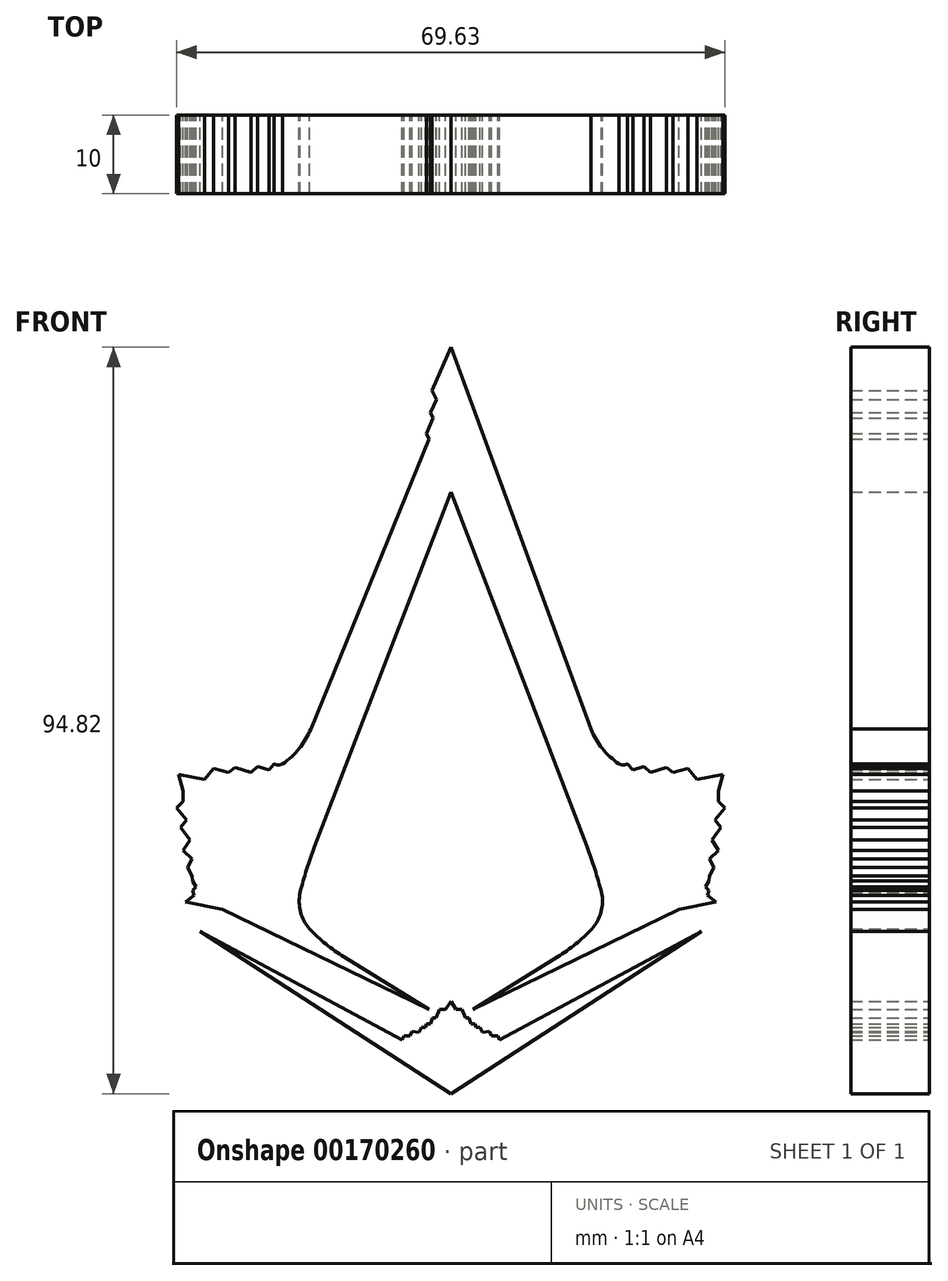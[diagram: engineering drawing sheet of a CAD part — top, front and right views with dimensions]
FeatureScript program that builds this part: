
annotation { "Feature Type Name" : "Feature", "Feature Type Description" : "" }
export const myFeature = defineFeature(function(context is Context, id is Id, definition is map)
    precondition{}
    {
        {
            var Q0;
            Q0=qCreatedBy(makeId("Front.planeOp"),FACE);
            var sketch = newSketch(context, id + "F0", { "sketchPlane" : qUnion([Q0])});
            skLineSegment(sketch, "E0", {"start": v(-37.8, 97.98) * mm, "end": v(-40.16, 92.47) * mm});
            skLineSegment(sketch, "E1", {"start": v(-40.16, 92.47) * mm, "end": v(-39.64, 91.37) * mm});
            skLineSegment(sketch, "E2", {"start": v(-39.64, 91.37) * mm, "end": v(-40.37, 89.66) * mm});
            skLineSegment(sketch, "E3", {"start": v(-40.37, 89.66) * mm, "end": v(-40.05, 88.98) * mm});
            skLineSegment(sketch, "E4", {"start": v(-40.05, 88.98) * mm, "end": v(-40.89, 87.02) * mm});
            skLineSegment(sketch, "E5", {"start": v(-40.89, 87.02) * mm, "end": v(-40.57, 86.34) * mm});
            skLineSegment(sketch, "E6", {"start": v(-40.57, 86.34) * mm, "end": v(-55.58, 49.5) * mm});
            skArc(sketch, "E7", {"start": v(-59.18, 45.05) * mm, "mid": v(-57.05, 47) * mm, "end": v(-55.58, 49.5) * mm});
            skArc(sketch, "E8", {"start": v(-60.27, 45.05) * mm, "mid": v(-59.72, 44.92) * mm, "end": v(-59.18, 45.05) * mm});
            skLineSegment(sketch, "E9", {"start": v(-60.27, 45.05) * mm, "end": v(-60.91, 44.28) * mm});
            skLineSegment(sketch, "E10", {"start": v(-60.91, 44.28) * mm, "end": v(-62.37, 44.73) * mm});
            skLineSegment(sketch, "E11", {"start": v(-62.37, 44.73) * mm, "end": v(-63.16, 43.94) * mm});
            skLineSegment(sketch, "E12", {"start": v(-63.16, 43.94) * mm, "end": v(-65.22, 44.58) * mm});
            skLineSegment(sketch, "E13", {"start": v(-65.22, 44.58) * mm, "end": v(-66.03, 43.94) * mm});
            skLineSegment(sketch, "E14", {"start": v(-66.03, 43.94) * mm, "end": v(-67.9, 44.5) * mm});
            skLineSegment(sketch, "E15", {"start": v(-67.9, 44.5) * mm, "end": v(-69.09, 43.07) * mm});
            skLineSegment(sketch, "E16", {"start": v(-69.09, 43.07) * mm, "end": v(-72.39, 43.71) * mm});
            skLineSegment(sketch, "E17", {"start": v(-72.39, 43.71) * mm, "end": v(-71.83, 41.6) * mm});
            skLineSegment(sketch, "E18", {"start": v(-71.83, 41.6) * mm, "end": v(-71.78, 40.3) * mm});
            skLineSegment(sketch, "E19", {"start": v(-71.78, 40.3) * mm, "end": v(-72.62, 39.43) * mm});
            skLineSegment(sketch, "E20", {"start": v(-72.62, 39.43) * mm, "end": v(-71.38, 37.91) * mm});
            skLineSegment(sketch, "E21", {"start": v(-71.38, 37.91) * mm, "end": v(-72.13, 37) * mm});
            skLineSegment(sketch, "E22", {"start": v(-72.13, 37) * mm, "end": v(-70.95, 35.4) * mm});
            skLineSegment(sketch, "E23", {"start": v(-70.95, 35.4) * mm, "end": v(-71.83, 34.07) * mm});
            skLineSegment(sketch, "E24", {"start": v(-71.83, 34.07) * mm, "end": v(-70.66, 32.96) * mm});
            skLineSegment(sketch, "E25", {"start": v(-70.66, 32.96) * mm, "end": v(-71.26, 31.9) * mm});
            skLineSegment(sketch, "E26", {"start": v(-71.26, 31.9) * mm, "end": v(-70.66, 30.84) * mm});
            skLineSegment(sketch, "E27", {"start": v(-70.66, 30.84) * mm, "end": v(-70.63, 30.2) * mm});
            skLineSegment(sketch, "E28", {"start": v(-70.63, 30.2) * mm, "end": v(-70.16, 29.45) * mm});
            skLineSegment(sketch, "E29", {"start": v(-70.16, 29.45) * mm, "end": v(-70.6, 28.95) * mm});
            skLineSegment(sketch, "E30", {"start": v(-70.6, 28.95) * mm, "end": v(-70.44, 28.36) * mm});
            skLineSegment(sketch, "E31", {"start": v(-70.44, 28.36) * mm, "end": v(-71.46, 27.5) * mm});
            skLineSegment(sketch, "E32", {"start": v(-71.46, 27.5) * mm, "end": v(-66.77, 26.58) * mm});
            skLineSegment(sketch, "E33", {"start": v(-69.65, 23.77) * mm, "end": v(-43.99, 10.02) * mm});
            skLineSegment(sketch, "E34", {"start": v(-43.99, 10.02) * mm, "end": v(-43.77, 10.47) * mm});
            skLineSegment(sketch, "E35", {"start": v(-43.77, 10.47) * mm, "end": v(-42.96, 10.47) * mm});
            skLineSegment(sketch, "E36", {"start": v(-42.96, 10.47) * mm, "end": v(-42.71, 11.09) * mm});
            skLineSegment(sketch, "E37", {"start": v(-42.71, 11.09) * mm, "end": v(-41.82, 10.97) * mm});
            skLineSegment(sketch, "E38", {"start": v(-41.82, 10.97) * mm, "end": v(-41.54, 11.59) * mm});
            skLineSegment(sketch, "E39", {"start": v(-41.54, 11.59) * mm, "end": v(-41.03, 11.59) * mm});
            skLineSegment(sketch, "E40", {"start": v(-41.03, 11.59) * mm, "end": v(-40.9, 12.05) * mm});
            skLineSegment(sketch, "E41", {"start": v(-40.9, 12.05) * mm, "end": v(-40.38, 12.05) * mm});
            skLineSegment(sketch, "E42", {"start": v(-40.38, 12.05) * mm, "end": v(-40.14, 12.8) * mm});
            skLineSegment(sketch, "E43", {"start": v(-40.14, 12.8) * mm, "end": v(-39.68, 12.8) * mm});
            skLineSegment(sketch, "E44", {"start": v(-39.68, 12.8) * mm, "end": v(-39.25, 13.9) * mm});
            skLineSegment(sketch, "E45", {"start": v(-39.25, 13.9) * mm, "end": v(-38.48, 13.9) * mm});
            skLineSegment(sketch, "E46", {"start": v(-38.48, 13.9) * mm, "end": v(-37.8, 14.86) * mm});
            skLineSegment(sketch, "E47", {"start": v(-69.65, 23.77) * mm, "end": v(-37.8, 3.16) * mm});
            skLineSegment(sketch, "E48", {"start": v(-66.77, 26.58) * mm, "end": v(-40.6, 13.87) * mm});
            skLineSegment(sketch, "E49", {"start": v(-40.6, 13.87) * mm, "end": v(-51.36, 20.54) * mm});
            skArc(sketch, "E50", {"start": v(-55.76, 24.08) * mm, "mid": v(-53.67, 22.17) * mm, "end": v(-51.36, 20.54) * mm});
            skArc(sketch, "E51", {"start": v(-56.96, 28.7) * mm, "mid": v(-56.89, 26.25) * mm, "end": v(-55.76, 24.08) * mm});
            skLineSegment(sketch, "E52", {"start": v(-37.8, 79.6) * mm, "end": v(-55.1, 34.54) * mm});
            skArc(sketch, "E53", {"start": v(-55.1, 34.54) * mm, "mid": v(-56.1, 31.65) * mm, "end": v(-56.96, 28.7) * mm});
            skLineSegment(sketch, "E54.MirrorCS", {"start": v(-32.64, 10.47) * mm, "end": v(-32.9, 11.09) * mm});
            skLineSegment(sketch, "E55.MirrorCS", {"start": v(-35.23, 12.05) * mm, "end": v(-35.47, 12.8) * mm});
            skLineSegment(sketch, "E56.MirrorCS", {"start": v(-33.79, 10.97) * mm, "end": v(-34.07, 11.59) * mm});
            skLineSegment(sketch, "E57.MirrorCS", {"start": v(-36.36, 13.9) * mm, "end": v(-37.13, 13.9) * mm});
            skLineSegment(sketch, "E58.MirrorCS", {"start": v(-35.47, 12.8) * mm, "end": v(-35.92, 12.8) * mm});
            skLineSegment(sketch, "E59.MirrorCS", {"start": v(-34.57, 11.59) * mm, "end": v(-34.71, 12.05) * mm});
            skLineSegment(sketch, "E60.MirrorCS", {"start": v(-35.92, 12.8) * mm, "end": v(-36.36, 13.9) * mm});
            skLineSegment(sketch, "E61.MirrorCS", {"start": v(-32.9, 11.09) * mm, "end": v(-33.79, 10.97) * mm});
            skLineSegment(sketch, "E62.MirrorCS", {"start": v(-34.07, 11.59) * mm, "end": v(-34.57, 11.59) * mm});
            skLineSegment(sketch, "E63.MirrorCS", {"start": v(-31.83, 10.47) * mm, "end": v(-32.64, 10.47) * mm});
            skLineSegment(sketch, "E64.MirrorCS", {"start": v(-34.71, 12.05) * mm, "end": v(-35.23, 12.05) * mm});
            skLineSegment(sketch, "E65.MirrorCS", {"start": v(-4.22, 37.91) * mm, "end": v(-3.47, 37) * mm});
            skLineSegment(sketch, "E66.MirrorCS", {"start": v(-3.21, 43.71) * mm, "end": v(-3.77, 41.6) * mm});
            skLineSegment(sketch, "E67.MirrorCS", {"start": v(-5.01, 28.95) * mm, "end": v(-5.17, 28.36) * mm});
            skLineSegment(sketch, "E68.MirrorCS", {"start": v(-4.34, 31.9) * mm, "end": v(-4.94, 30.84) * mm});
            skLineSegment(sketch, "E69.MirrorCS", {"start": v(-3.77, 41.6) * mm, "end": v(-3.82, 40.3) * mm});
            skLineSegment(sketch, "E70.MirrorCS", {"start": v(-3.47, 37) * mm, "end": v(-4.66, 35.4) * mm});
            skLineSegment(sketch, "E71.MirrorCS", {"start": v(-5.17, 28.36) * mm, "end": v(-4.14, 27.5) * mm});
            skLineSegment(sketch, "E72.MirrorCS", {"start": v(-4.94, 32.96) * mm, "end": v(-4.34, 31.9) * mm});
            skLineSegment(sketch, "E73.MirrorCS", {"start": v(-10.38, 44.58) * mm, "end": v(-9.57, 43.94) * mm});
            skLineSegment(sketch, "E74.MirrorCS", {"start": v(-2.99, 39.43) * mm, "end": v(-4.22, 37.91) * mm});
            skLineSegment(sketch, "E75.MirrorCS", {"start": v(-13.23, 44.73) * mm, "end": v(-12.45, 43.94) * mm});
            skArc(sketch, "E76.MirrorCS", {"start": v(-15.33, 45.05) * mm, "mid": v(-15.88, 44.92) * mm, "end": v(-16.43, 45.05) * mm});
            skLineSegment(sketch, "E77.MirrorCS", {"start": v(-15.33, 45.05) * mm, "end": v(-14.7, 44.28) * mm});
            skLineSegment(sketch, "E78.MirrorCS", {"start": v(-12.45, 43.94) * mm, "end": v(-10.38, 44.58) * mm});
            skLineSegment(sketch, "E79.MirrorCS", {"start": v(-31.62, 10.02) * mm, "end": v(-31.83, 10.47) * mm});
            skLineSegment(sketch, "E80.MirrorCS", {"start": v(-14.7, 44.28) * mm, "end": v(-13.23, 44.73) * mm});
            skLineSegment(sketch, "E81.MirrorCS", {"start": v(-4.98, 30.2) * mm, "end": v(-5.45, 29.45) * mm});
            skLineSegment(sketch, "E82.MirrorCS", {"start": v(-4.94, 30.84) * mm, "end": v(-4.98, 30.2) * mm});
            skLineSegment(sketch, "E83.MirrorCS", {"start": v(-7.7, 44.5) * mm, "end": v(-6.52, 43.07) * mm});
            skLineSegment(sketch, "E84.MirrorCS", {"start": v(-37.13, 13.9) * mm, "end": v(-37.8, 14.86) * mm});
            skLineSegment(sketch, "E85.MirrorCS", {"start": v(-3.77, 34.07) * mm, "end": v(-4.94, 32.96) * mm});
            skLineSegment(sketch, "E86.MirrorCS", {"start": v(-3.82, 40.3) * mm, "end": v(-2.99, 39.43) * mm});
            skLineSegment(sketch, "E87.MirrorCS", {"start": v(-4.66, 35.4) * mm, "end": v(-3.77, 34.07) * mm});
            skLineSegment(sketch, "E88.MirrorCS", {"start": v(-5.45, 29.45) * mm, "end": v(-5.01, 28.95) * mm});
            skLineSegment(sketch, "E89.MirrorCS", {"start": v(-9.57, 43.94) * mm, "end": v(-7.7, 44.5) * mm});
            skLineSegment(sketch, "E90.MirrorCS", {"start": v(-6.52, 43.07) * mm, "end": v(-3.21, 43.71) * mm});
            skArc(sketch, "E91.MirrorCS", {"start": v(-20.51, 34.54) * mm, "mid": v(-19.5, 31.65) * mm, "end": v(-18.65, 28.7) * mm});
            skLineSegment(sketch, "E92.MirrorCS", {"start": v(-35, 13.87) * mm, "end": v(-24.24, 20.54) * mm});
            skLineSegment(sketch, "E93.MirrorCS", {"start": v(-5.95, 23.77) * mm, "end": v(-31.62, 10.02) * mm});
            skArc(sketch, "E94.MirrorCS", {"start": v(-18.65, 28.7) * mm, "mid": v(-18.72, 26.25) * mm, "end": v(-19.85, 24.08) * mm});
            skLineSegment(sketch, "E95.MirrorCS", {"start": v(-5.95, 23.77) * mm, "end": v(-37.8, 3.16) * mm});
            skArc(sketch, "E96.MirrorCS", {"start": v(-16.43, 45.05) * mm, "mid": v(-18.55, 47) * mm, "end": v(-20.02, 49.5) * mm});
            skLineSegment(sketch, "E97.MirrorCS", {"start": v(-8.83, 26.58) * mm, "end": v(-35, 13.87) * mm});
            skArc(sketch, "E98.MirrorCS", {"start": v(-19.85, 24.08) * mm, "mid": v(-21.93, 22.17) * mm, "end": v(-24.24, 20.54) * mm});
            skLineSegment(sketch, "E99.MirrorCS", {"start": v(-4.14, 27.5) * mm, "end": v(-8.83, 26.58) * mm});
            skLineSegment(sketch, "E100", {"start": v(-37.8, 97.98) * mm, "end": v(-20.02, 49.5) * mm});
            skLineSegment(sketch, "E101.MirrorCS", {"start": v(-37.8, 79.6) * mm, "end": v(-20.51, 34.54) * mm});
            skSolve(sketch);
        }
        {
            var Q0;
            Q0=makeQuery(id+"F0.imprint","IMPRINT",FACE,{"disambiguationData":[TD([[makeQuery(id+"F0.imprint","IMPRINT",EDGE,{"derivedFrom":sQuery(id+"F0.wireOp",EDGE,"E0")}),1.0]])]});
            var Q1;
            Q1=makeQuery(id+"F0.imprint","IMPRINT",FACE,{"disambiguationData":[TD([[makeQuery(id+"F0.imprint","IMPRINT",EDGE,{"derivedFrom":sQuery(id+"F0.wireOp",EDGE,"E33")}),-1.0]])]});
            extrude(context, id + "F1", {"entities" : qUnion([Q0, Q1]), "depth" : 10 * mm});
        }
    });
